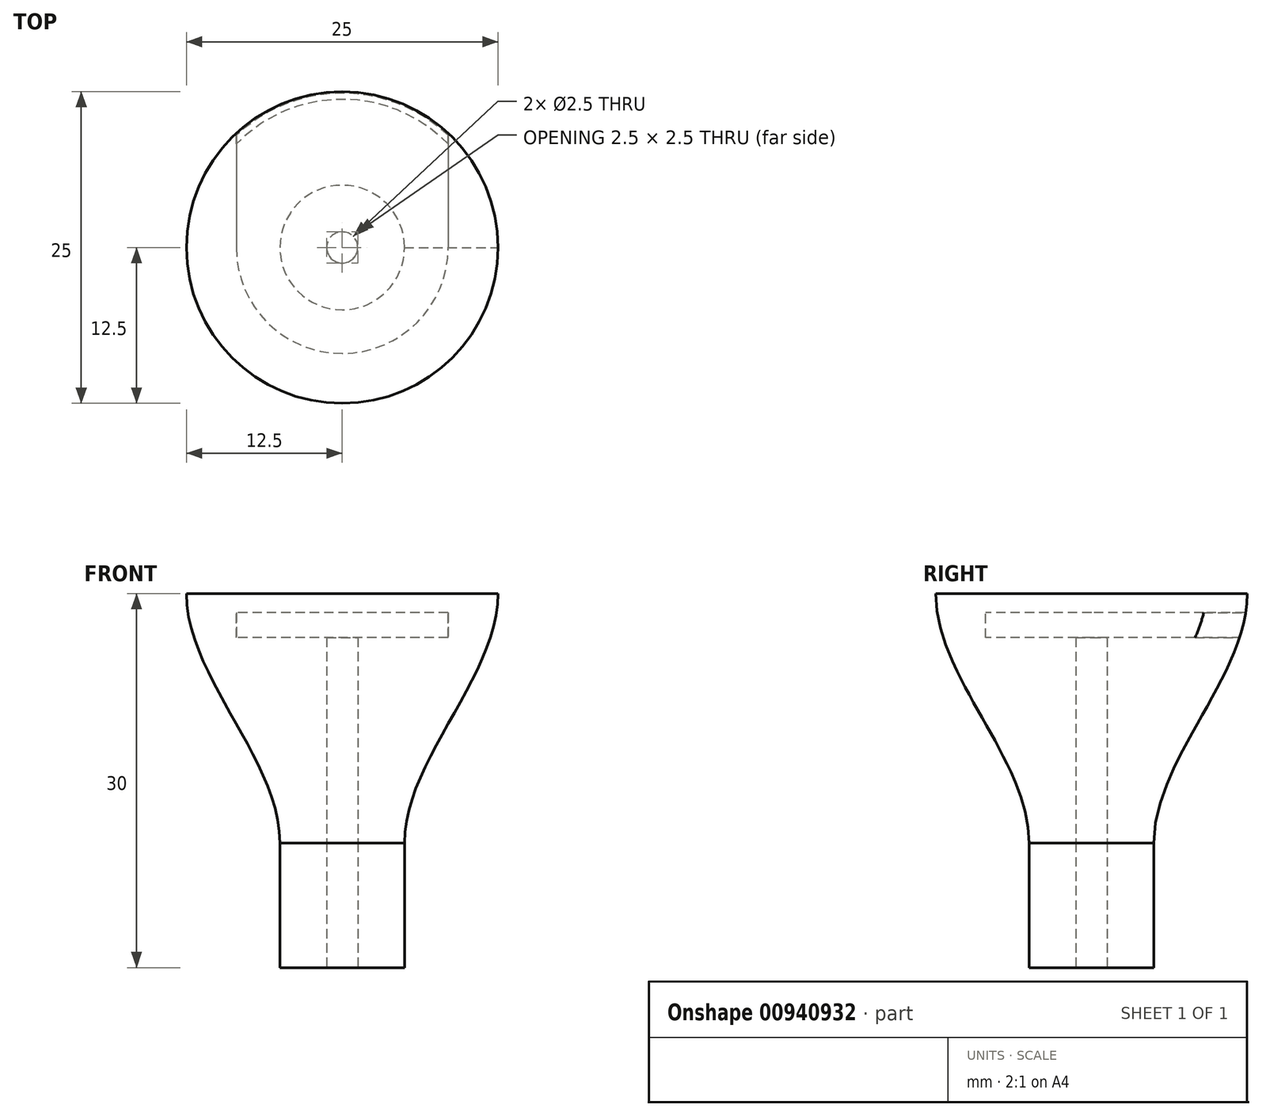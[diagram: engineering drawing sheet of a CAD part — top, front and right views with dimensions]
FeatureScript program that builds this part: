
annotation { "Feature Type Name" : "Feature", "Feature Type Description" : "" }
export const myFeature = defineFeature(function(context is Context, id is Id, definition is map)
    precondition{}
    {
        {
            var Q0;
            Q0=qCreatedBy(makeId("Top.planeOp"),FACE);
            var sketch = newSketch(context, id + "F0", { "sketchPlane" : qUnion([Q0])});
            skCircle(sketch, "E0", {"center": v(0, 0) * mm, "radius": 5 * mm});
            skSolve(sketch);
        }
        {
            var Q0;
            Q0 = qSketchRegion(id + "F0", true);
            extrude(context, id + "F1", {"entities" : qUnion([Q0]), "depth" : 10 * mm, "offsetDistance" : 25 * mm});
        }
        {
            var Q0;
            Q0=makeQuery(id+"F1.opExtrude","CAP_FACE",FACE,{"disambiguationData":[OSD([sQuery(id+"F0.wireOp",EDGE,"E0")])],"isStart":true});
            var sketch = newSketch(context, id + "F2", { "sketchPlane" : qUnion([Q0])});
            skCircle(sketch, "E1", {"center": v(0, 0) * mm, "radius": 1.25 * mm});
            skSolve(sketch);
        }
        {
            var Q0;
            Q0=qCreatedBy(makeId("Top.planeOp"),FACE);
            cPlane(context, id + "F3", {"entities" : qUnion([Q0]), "cplaneType" : CPlaneType.OFFSET, "offset" : 30 * mm, "width" : 150 * mm, "height" : 150 * mm});
        }
        {
            var Q0;
            Q0=qCreatedBy(id+"F3.planeOp",FACE);
            var sketch = newSketch(context, id + "F4", { "sketchPlane" : qUnion([Q0])});
            skCircle(sketch, "E2", {"center": v(0, 0) * mm, "radius": 12.5 * mm});
            skSolve(sketch);
        }
        {
            var Q0;
            Q0=makeQuery(id+"F1.opExtrude","CAP_FACE",FACE,{"disambiguationData":[OSD([sQuery(id+"F0.wireOp",EDGE,"E0")])],"isStart":false});
            var Q1;
            Q1=makeQuery(id+"F4.imprint","IMPRINT",FACE,{"disambiguationData":[TD([[makeQuery(id+"F4.imprint","IMPRINT",EDGE,{"derivedFrom":sQuery(id+"F4.wireOp",EDGE,"E2")}),1.0]])]});
            loft(context, id + "F5", {"startCondition" : LoftEndDerivativeType.NORMAL_TO_PROFILE, "startMagnitude" : 1, "endCondition" : LoftEndDerivativeType.NORMAL_TO_PROFILE, "endMagnitude" : 1, "sheetProfilesArray" : [{ "sheetProfileEntities" : qUnion([Q0]) }, { "sheetProfileEntities" : qUnion([Q1]) }]});
        }
        {
            var Q0;
            Q0=qCreatedBy(makeId("Front.planeOp"),FACE);
            var sketch = newSketch(context, id + "F6", { "sketchPlane" : qUnion([Q0])});
            skLineSegment(sketch, "E3.bottom", {"start": v(-8.5, 28.46) * mm, "end": v(8.5, 28.46) * mm});
            skLineSegment(sketch, "E3.top", {"start": v(-8.5, 26.46) * mm, "end": v(8.5, 26.46) * mm});
            skLineSegment(sketch, "E3.left", {"start": v(-8.5, 28.46) * mm, "end": v(-8.5, 26.46) * mm});
            skLineSegment(sketch, "E3.right", {"start": v(8.5, 28.46) * mm, "end": v(8.5, 26.46) * mm});
            skPoint(sketch, "E4", {"position": v(0, 28.46) * mm});
            skLineSegment(sketch, "E5", {"start": v(0, 52.72) * mm, "end": v(0, 0) * mm, "construction": true});
            skSolve(sketch);
        }
        {
            var Q0;
            Q0 = qSketchRegion(id + "F6", true);
            extrude(context, id + "F7", {"entities" : qUnion([Q0]), "operationType" : NewBodyOperationType.REMOVE, "endBound" : BoundingType.THROUGH_ALL, "oppositeDirection" : true, "depth" : 25 * mm, "offsetDistance" : 25 * mm});
        }
        {
            var Q0;
            Q0=qCreatedBy(makeId("Front.planeOp"),FACE);
            var sketch = newSketch(context, id + "F8", { "sketchPlane" : qUnion([Q0])});
            skLineSegment(sketch, "E6.bottom", {"start": v(0, 28.46) * mm, "end": v(8.5, 28.46) * mm});
            skLineSegment(sketch, "E6.top", {"start": v(0, 26.46) * mm, "end": v(8.5, 26.46) * mm});
            skLineSegment(sketch, "E6.left", {"start": v(0, 28.46) * mm, "end": v(0, 26.46) * mm});
            skLineSegment(sketch, "E6.right", {"start": v(8.5, 28.46) * mm, "end": v(8.5, 26.46) * mm});
            skSolve(sketch);
        }
        {
            var Q0;
            Q0 = qSketchRegion(id + "F8", true);
            var Q1;
            Q1=sQuery(id+"F6.wireOp",EDGE,"E5");
            revolve(context, id + "F9", {"operationType" : NewBodyOperationType.REMOVE, "surfaceOperationType" : NewSurfaceOperationType.NEW, "entities" : qUnion([Q0]), "axis" : qUnion([Q1]), "revolveType" : RevolveType.FULL});
        }
        {
            var Q0;
            Q0 = qSketchRegion(id + "F2", true);
            var Q1;
            Q1=makeQuery(id+"F9.boolean.opBoolean","MERGE",FACE,{"derivedFrom":[makeQuery(id+"F7.boolean.opBoolean","COPY",FACE,{"derivedFrom":makeQuery(id+"F7.opExtrude","SWEPT_FACE",FACE,{"disambiguationData":[OSD([sQuery(id+"F6.wireOp",EDGE,"E3.top")])]})})],"fromTools":[makeQuery(id+"F9.opRevolve","SWEPT_FACE",FACE,{"disambiguationData":[OSD([sQuery(id+"F8.wireOp",EDGE,"E6.top")])]})]});
            extrude(context, id + "F10", {"entities" : qUnion([Q0]), "operationType" : NewBodyOperationType.REMOVE, "endBound" : BoundingType.UP_TO_SURFACE, "oppositeDirection" : true, "depth" : 25 * mm, "endBoundEntityFace" : qUnion([Q1]), "offsetDistance" : 25 * mm});
        }
    });
